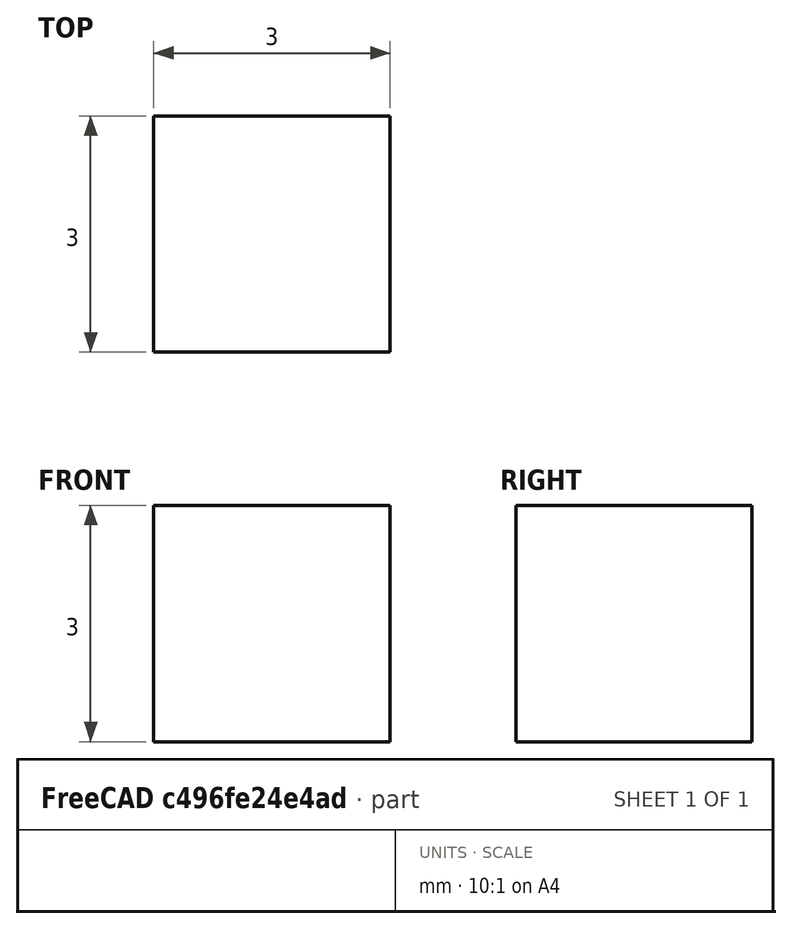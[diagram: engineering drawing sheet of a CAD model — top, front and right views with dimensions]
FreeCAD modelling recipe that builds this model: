
FCSTD DOCUMENT  (FreeCAD 1.0R39319 (Git))
Label: MAGNET-SQ3
License: All rights reserved
LicenseURL: http://en.wikipedia.org/wiki/All_rights_reserved
objects: TechDraw::DrawProjGroupItem×3, TechDraw::DrawViewDimension×3, PartDesign::Plane×2, TechDraw::DrawGeomHatch×2, TechDraw::DrawViewBalloon×2, TechDraw::DrawViewAnnotation×1, Sketcher::SketchObject×1, PartDesign::Pad×1, PartDesign::Mirrored×1, TechDraw::DrawSVGTemplate×1, PartDesign::Line×1, PartDesign::Body×1, TechDraw::DrawProjGroup×1, TechDraw::DrawPage×1
note: 15 computed .brp shape members not serialized (recipe doc carries the construction recipe); baked Part::Feature solids carry a one-line shape summary decoded from their .brp

FEATURE [TechDraw::DrawViewAnnotation] Annotation004
  Font = osifont
  LineSpace = 80
  LockPosition = false
  MaxWidth = -1
  Rotation = 0
  ScaleType = 1
  Text = Minimum Magnet Grade: N52
  TextSize = 5
  TextStyle = 0
  X = 106.281
  Y = 175.798
FEATURE [Sketcher::SketchObject] Sketch002
  ArcFitTolerance = 0
  AttachmentSupport = -> [XY_Plane003]
  FullyConstrained = true
  MakeInternals = false
  MapMode = 5
  sketch-geometry (6):
    g0: LineSegment StartX=1.5 StartY=1.5 StartZ=0 EndX=0 EndY=1.5 EndZ=0
    g1: LineSegment StartX=0 StartY=1.5 StartZ=0 EndX=0 EndY=-1.5 EndZ=0
    g2: LineSegment StartX=0 StartY=-1.5 StartZ=0 EndX=1.5 EndY=-1.5 EndZ=0
    g3: LineSegment StartX=1.5 StartY=-1.5 StartZ=0 EndX=1.5 EndY=1.5 EndZ=0
    g4: LineSegment [constr] StartX=0 StartY=0 StartZ=0 EndX=1.5 EndY=1.5 EndZ=0
    g5: LineSegment [constr] StartX=1.5 StartY=-1.5 StartZ=0 EndX=0 EndY=0 EndZ=0
  constraints (16):
    c: Coincident(g0,g1)
    c: Coincident(g1,g2)
    c: Coincident(g2,g3)
    c: Coincident(g3,g0)
    c: Horizontal(g0)
    c: Horizontal(g2)
    c: Vertical(g1)
    c: Vertical(g3)
    c: PointOnObject(g1,g-2)
    c: DistanceY(g3,g3) = 3
    c: Coincident(g4,g-1)
    c: Coincident(g4,g0)
    c: Coincident(g5,g2)
    c: Coincident(g5,g4)
    c: Equal(g5,g4)
    c: DistanceX(g0,g0) = 1.5
FEATURE [PartDesign::Pad] Pad002  label="CubeN"
  Direction = (0,0,1)
  Length = 3
  Length2 = 10
  Profile = -> Sketch002
  ReferenceAxis = -> Sketch002 [N_Axis]
  Suppressed = false
  Type = 0
FEATURE [PartDesign::Mirrored] Mirrored001
  BaseFeature = -> Pad002
  MirrorPlane = -> Sketch002 [V_Axis]
  Originals = -> [Pad002]
  Suppressed = false
  TransformMode = 0
FEATURE [TechDraw::DrawSVGTemplate] Template001
  EditableTexts = Designed_by_Name=Designed by Name; Drawing_number=Drawing number; FC-Date=Date; FC-SC=Scale; FC-SH=Sheet; FC-Title=Title; Subtitle=Subtitle; Weight=Weight
  Height = 210
  Orientation = 1
  Template = /snap/freecad/759/usr/share/Mod/TechDraw/Templates/A4_LandscapeTD.svg
  Width = 297
FEATURE [PartDesign::Plane] Plane_1
  Length = 100
  ResizeMode = 1
  Width = 100
FEATURE [PartDesign::Plane] Plane_2
  AttachmentSupport = -> [Mirrored001]
  Length = 100
  MapMode = 5
  Placement = pos=(0,1.5,0) rot=(0,0.707107,0.707107;3.14159rad)
  ResizeMode = 1
  Width = 100
FEATURE [PartDesign::Line] Axis_2
  AttacherType = Attacher::AttachEngineLine
  AttachmentSupport = -> [Mirrored001]
  Length = 200
  MapMode = 29
  Placement = pos=(0,1.5,0) rot=(0.57735,0.57735,0.57735;2.0944rad)
  ResizeMode = 1
FEATURE [PartDesign::Body] Body002  label="MAGNET-SQ3"
  AllowCompound = false
  Group = -> [Sketch002,Pad002,Mirrored001,Plane_1,Plane_2,Axis_2]
  Origin = -> Origin003
  Tip = -> Mirrored001
FEATURE [TechDraw::DrawProjGroupItem] ProjItem009  label="Front001"
  CoarseView = false
  Direction = (0,-1,0)
  Focus = 100
  HardHidden = false
  IsoCount = 0
  IsoHidden = false
  IsoVisible = false
  LockPosition = true
  Perspective = false
  Rotation = 0
  RotationVector = (1,0,0)
  ScaleType = 2
  ScrubCount = 0
  SeamHidden = false
  SeamVisible = false
  SmoothHidden = false
  SmoothVisible = true
  Source = -> [Body002]
  Type = 0
  X = 0
  XDirection = (1,0,0)
  Y = 0
FEATURE [TechDraw::DrawProjGroupItem] ProjItem010  label="Left"
  CoarseView = false
  Direction = (-1,-1e-16,0)
  Focus = 100
  HardHidden = false
  IsoCount = 0
  IsoHidden = false
  IsoVisible = false
  LockPosition = false
  Perspective = false
  Rotation = 0
  RotationVector = (1,0,0)
  ScaleType = 2
  ScrubCount = 0
  SeamHidden = false
  SeamVisible = false
  SmoothHidden = false
  SmoothVisible = true
  Source = -> [Body002]
  Type = 1
  X = 48.1066
  XDirection = (1e-16,-1,0)
  Y = 0
FEATURE [TechDraw::DrawProjGroupItem] ProjItem011  label="FrontBottomLeft"
  CoarseView = false
  Direction = (-0.57735,-0.57735,-0.57735)
  Focus = 100
  HardHidden = false
  IsoCount = 0
  IsoHidden = false
  IsoVisible = false
  LockPosition = false
  Perspective = false
  Rotation = 0
  RotationVector = (1,0,0)
  ScaleType = 2
  ScrubCount = 0
  SeamHidden = false
  SeamVisible = false
  SmoothHidden = false
  SmoothVisible = true
  Source = -> [Body002]
  Type = 8
  X = 48.1066
  XDirection = (0.707107,-0.707107,0)
  Y = 49.7474
FEATURE [TechDraw::DrawProjGroup] ProjGroup001
  Anchor = -> ProjItem009
  AutoDistribute = true
  LockPosition = false
  ProjectionType = 0
  Rotation = 0
  Scale = 5
  ScaleType = 0
  Source = -> [Body002]
  Views = -> [ProjItem009,ProjItem010,ProjItem011]
  X = 50
  Y = 75
  spacingX = 30
  spacingY = 30
FEATURE [TechDraw::DrawGeomHatch] GeomHatch  label="GeomHatchFX1"
  FilePattern = /snap/freecad/759/usr/share/Mod/TechDraw/PAT/FCPAT.pat
  NamePattern = Diamond
  PatternOffset = (0,0,0)
  PatternRotation = 0
  ScalePattern = 1
  Source = -> ProjItem011 [Face1,Face4,Face3]
FEATURE [TechDraw::DrawGeomHatch] GeomHatch001  label="GeomHatch001FX2"
  FilePattern = /snap/freecad/759/usr/share/Mod/TechDraw/PAT/FCPAT.pat
  NamePattern = Diamond
  PatternOffset = (0,0,0)
  PatternRotation = 0
  ScalePattern = 1
  Source = -> ProjItem011 [Face2,Face5]
FEATURE [TechDraw::DrawViewDimension] Dimension
  AngleOverride = false
  Arbitrary = false
  ArbitraryTolerances = false
  EqualTolerance = true
  ExtensionAngle = 0
  FormatSpec = %.2w
  FormatSpecOverTolerance = %+.2w
  FormatSpecUnderTolerance = %+.2w
  Inverted = false
  LineAngle = 0
  LockPosition = false
  MeasureType = 1
  OverTolerance = 0
  References2D = -> [ProjItem009]
  Rotation = 0
  Scale = 5
  ScaleType = 0
  TheoreticalExact = false
  Type = 1
  UnderTolerance = 0
  X = -0.179028
  Y = 26.2916
FEATURE [TechDraw::DrawViewDimension] Dimension001
  AngleOverride = false
  Arbitrary = false
  ArbitraryTolerances = false
  EqualTolerance = true
  ExtensionAngle = 0
  FormatSpec = %.2w
  FormatSpecOverTolerance = %+.2w
  FormatSpecUnderTolerance = %+.2w
  Inverted = false
  LineAngle = 0
  LockPosition = false
  MeasureType = 1
  OverTolerance = 0
  References2D = -> [ProjItem009]
  Rotation = 0
  Scale = 5
  ScaleType = 0
  TheoreticalExact = false
  Type = 2
  UnderTolerance = 0
  X = -21.1061
  Y = 1.96292
FEATURE [TechDraw::DrawViewDimension] Dimension002
  AngleOverride = false
  Arbitrary = false
  ArbitraryTolerances = false
  EqualTolerance = true
  ExtensionAngle = 0
  FormatSpec = %.2w
  FormatSpecOverTolerance = %+.2w
  FormatSpecUnderTolerance = %+.2w
  Inverted = false
  LineAngle = 0
  LockPosition = false
  MeasureType = 1
  OverTolerance = 0
  References2D = -> [ProjItem010]
  Rotation = 0
  Scale = 5
  ScaleType = 0
  TheoreticalExact = false
  Type = 1
  UnderTolerance = 0
  X = 0
  Y = 25.5754
FEATURE [TechDraw::DrawViewBalloon] Balloon
  BubbleShape = 6
  EndType = 1
  EndTypeScale = 1
  KinkLength = 5
  LockPosition = false
  OriginX = -2.9
  OriginY = 2
  Rotation = 0
  Scale = 5
  ScaleType = 0
  ShapeScale = 1
  SourceView = -> ProjItem011
  Text = North
  TextWrapLen = -1
  X = -6.66991
  Y = 2.71803
FEATURE [TechDraw::DrawViewBalloon] Balloon001
  BubbleShape = 6
  EndType = 1
  EndTypeScale = 1
  KinkLength = 5
  LockPosition = false
  OriginX = 3
  OriginY = -1.78
  Rotation = 0
  Scale = 5
  ScaleType = 0
  ShapeScale = 1
  SourceView = -> ProjItem011
  Text = South
  TextWrapLen = -1
  X = 6.86461
  Y = -2.29476
FEATURE [TechDraw::DrawPage] Page001  label="MAGNET-SQ3_Drawing"
  KeepUpdated = true
  NextBalloonIndex = 5
  ProjectionType = 0
  Scale = 5
  Template = -> Template001
  Views = -> [Annotation004,ProjGroup001,Dimension,Dimension001,Dimension002,Balloon,Balloon001]
